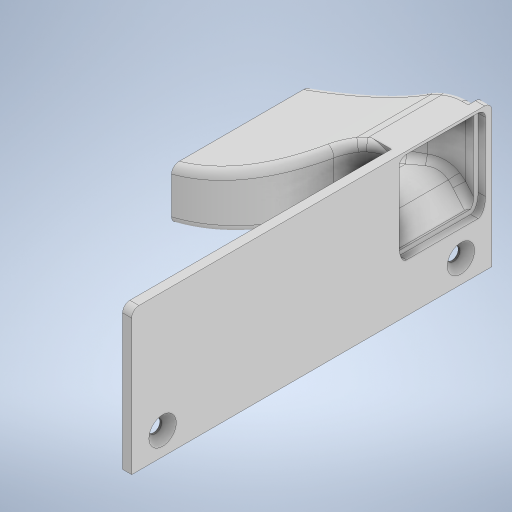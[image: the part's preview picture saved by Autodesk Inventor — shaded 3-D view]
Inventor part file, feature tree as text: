
AUTODESK INVENTOR PART (.ipt)
format: ipt  version: 2024 (Build 280153000, 153)  size: 836,096 bytes
history: native  units: mm
features: reference x28, sketch x13, extrude x10, other x7, plane x3, projected_geometry x3, loft x2, fillet x2, shell x1, chamfer x1
ambient origin geometry x8: Origin, YZ Plane, XZ Plane, XY Plane, X Axis, Y Axis, Z Axis, Center Point
bodies: Solid1 (feature_tree)
feature tree (70):
  extrude  "Extrusion1"  Depth=99.0mm
  plane  "Work Plane3"
  sketch  "Sketch2"  dims[d2=2.5mm d3=0.0mm d4=2.0mm]
  plane  "Work Plane2"
  sketch  "Sketch4"  dims[d13=7.0mm d14=10.0mm d15=1.0mm d16=1.0mm]
  loft  "Loft1"
  loft  "Loft4"
  fillet  "Fillet4"  Radius=2.0mm
  sketch  "Sketch6"  dims[d24=1.0mm d25=1.0mm]
  shell  "Shell1"  Thickness=1.0mm
  extrude  "Extrusion3"  Depth=1.0mm
  extrude  "Extrusion4"  Depth=1.0mm
  extrude  "Extrusion5"  Depth=1.0mm
  extrude  "Extrusion6"  TaperAngle=0.0deg  [1 undecoded]
  fillet  "Fillet5"  Radius=1.0mm
  extrude  "Extrusion7"  TaperAngle=0.0deg  [1 undecoded]
  extrude  "Extrusion8"  Depth=10.0mm
  extrude  "Extrusion9"  Depth=2.5mm TaperAngle=0.0deg
  extrude  "Extrusion11"  Depth=1.0mm TaperAngle=0.0deg
  chamfer  "Chamfer1"  Distance=2.5mm
  extrude  "Extrusion12"  Depth=2.0mm
  sketch  "Sketch1"  dims[d0=39.26mm d1=99.0mm]
  reference  "Reference1"
  reference  "Reference2"
  reference  "Reference3"
  reference  "Reference4"
  plane  "Work Plane1"
  sketch  "Sketch3"  dims[d5=0.0mm d6=2.0mm d9=2.0mm d10=1.0mm]
  reference  "Reference5"
  reference  "Reference6"
  reference  "Reference7"
  reference  "Reference8"
  reference  "Reference9"
  reference  "Reference10"
  reference  "Reference11"
  sketch  "Sketch5"  dims[d18=1.0mm d23=1.0mm]
  reference  "Reference12"
  reference  "Reference13"
  reference  "Reference14"
  reference  "Reference15"
  other  "Edges4"
  projected_geometry  "Projected Loop1"
  sketch  "Sketch7"  dims[d26=1.0mm d35=0.0mm]
  projected_geometry  "Projected Loop2"
  sketch  "Sketch8"  dims[d36=0.0mm d37=90.0deg d38=0.0mm d39=90.0deg d42=1.0mm d43=1.0mm]
  projected_geometry  "Projected Loop3"
  sketch  "Sketch9"  dims[d46=0.0mm d47=90.0deg d59=0.0mm d60=90.0deg]
  reference  "Reference16"
  reference  "Reference17"
  sketch  "Sketch10"  dims[d61=0.0mm d62=90.0deg d63=10.0mm]
  reference  "Reference18"
  reference  "Reference19"
  reference  "Reference20"
  reference  "Reference21"
  reference  "Reference22"
  reference  "Reference23"
  sketch  "Sketch11"  dims[d64=0.0mm d65=2.5mm d66=0.0mm]
  sketch  "Sketch13"  dims[d67=1.0mm d68=1.0mm d69=0.0mm d70=2.5mm d71=0.0mm]
  reference  "Reference28"
  reference  "Reference29"
  reference  "Reference30"
  reference  "Reference31"
  reference  "Reference32"
  sketch  "Sketch14"  dims[d72=0.0mm d73=0.0mm d74=2.0mm d75=3.5mm d76=3.5mm d77=2.5mm d78=0.0mm d79=2.0mm d80=0.0mm d81=1.0mm d82=2.0mm d83=1.0mm d84=1.0mm d85=2.0mm d86=0.0mm d89=2.0mm d90=0.0mm d91=2.0mm d92=2.0mm d93=45.0deg d94=2.0mm d95=0.0mm]
  parser-record x1  (decoder bookkeeping rows leaked as tree rows — omitted from the tree; the rows remain in map.json)
  other  "REV 3 assembly.iam"
  other  "TA07 ELECTRONICS MOUNT REV 3:1"
  other  "Top3518_3668_A02_3509_A01_0204:1"
  other  "Shroud Top:1"
  other  "Rear Exhaust Manifold:1"
note: 2 required parameter values undecoded (feature->parameter linkage not recoverable at this tier; creation-order binding heuristic only, values carry confidence <= 0.55)
note: 1 file-system path scrubbed to <path> (originals preserved in map.json)
